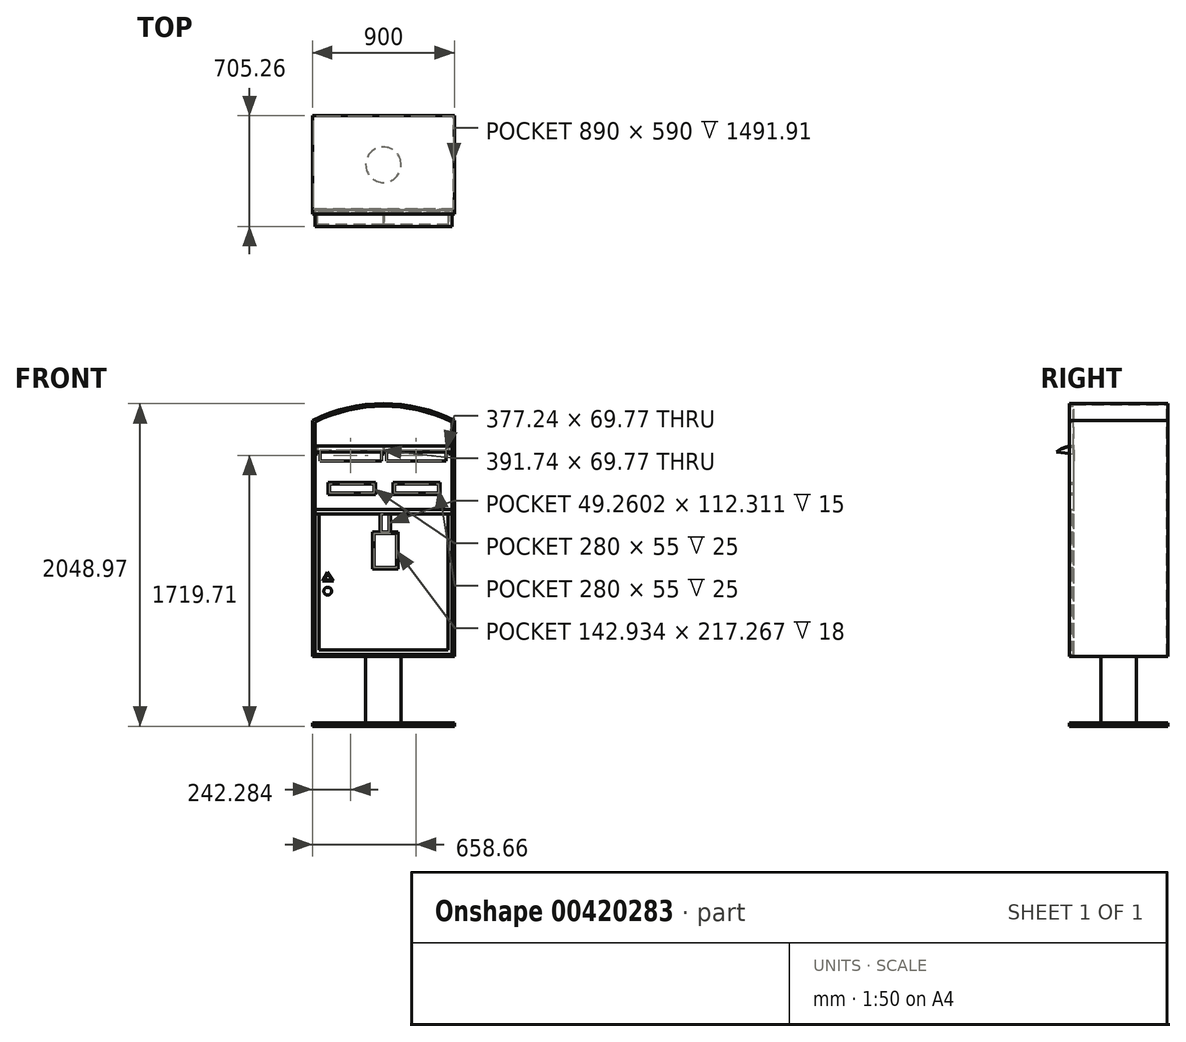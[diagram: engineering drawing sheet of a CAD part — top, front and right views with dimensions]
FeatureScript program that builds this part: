
annotation { "Feature Type Name" : "Feature", "Feature Type Description" : "" }
export const myFeature = defineFeature(function(context is Context, id is Id, definition is map)
    precondition{}
    {
        {
            var Q0;
            Q0=qCreatedBy(makeId("Front.planeOp"),FACE);
            var sketch = newSketch(context, id + "F0", { "sketchPlane" : qUnion([Q0])});
            skLineSegment(sketch, "E0.bottom", {"start": v(450, -750) * mm, "end": v(-450, -750) * mm});
            skLineSegment(sketch, "E0.left", {"start": v(450, -750) * mm, "end": v(450, 750) * mm});
            skLineSegment(sketch, "E0.right", {"start": v(-450, -750) * mm, "end": v(-450, 750) * mm});
            skPoint(sketch, "E0.middle", {"position": v(0, 0) * mm});
            skArc(sketch, "E1", {"start": v(450, 750) * mm, "mid": v(0, 856.97) * mm, "end": v(-450, 750) * mm});
            skLineSegment(sketch, "E2", {"start": v(-450, 750) * mm, "end": v(450, 750) * mm, "construction": true});
            skSolve(sketch);
        }
        {
            var Q0;
            Q0=makeQuery(id+"F0.imprint","IMPRINT",FACE,{"disambiguationData":[TD([[makeQuery(id+"F0.imprint","IMPRINT",EDGE,{"derivedFrom":sQuery(id+"F0.wireOp",EDGE,"E0.bottom")}),-1.0]])]});
            extrude(context, id + "F1", {"entities" : qUnion([Q0]), "depth" : 600 * mm});
        }
        {
            var Q0;
            Q0=makeQuery(id+"F1.opExtrude","CAP_FACE",FACE,{"disambiguationData":[OSD([sQuery(id+"F0.wireOp",EDGE,"E0.bottom"),sQuery(id+"F0.wireOp",EDGE,"E0.left"),sQuery(id+"F0.wireOp",EDGE,"E0.right"),sQuery(id+"F0.wireOp",EDGE,"E1")])],"isStart":true});
            shell(context, id + "F2", {"entities" : qUnion([Q0]), "thickness" : 5 * mm});
        }
        {
            var Q0;
            Q0=makeQuery(id+"F1.opExtrude","CAP_FACE",FACE,{"disambiguationData":[OSD([sQuery(id+"F0.wireOp",EDGE,"E0.bottom"),sQuery(id+"F0.wireOp",EDGE,"E0.left"),sQuery(id+"F0.wireOp",EDGE,"E0.right"),sQuery(id+"F0.wireOp",EDGE,"E1")])],"isStart":false});
            var sketch = newSketch(context, id + "F3", { "sketchPlane" : qUnion([Q0])});
            skLineSegment(sketch, "E3.0", {"start": v(435, -735) * mm, "end": v(435, 740.71) * mm});
            skLineSegment(sketch, "E3.1", {"start": v(-435, -735) * mm, "end": v(435, -735) * mm});
            skLineSegment(sketch, "E3.2", {"start": v(-435, 740.71) * mm, "end": v(-435, -735) * mm});
            skArc(sketch, "E3.3", {"start": v(435, 740.71) * mm, "mid": v(0, 841.97) * mm, "end": v(-435, 740.71) * mm});
            skSolve(sketch);
        }
        {
            var Q0;
            Q0=makeQuery(id+"F3.imprint","IMPRINT",FACE,{"disambiguationData":[TD([[makeQuery(id+"F3.imprint","IMPRINT",EDGE,{"derivedFrom":sQuery(id+"F3.wireOp",EDGE,"E3.0")}),-1.0]])]});
            extrude(context, id + "F4", {"entities" : qUnion([Q0]), "operationType" : NewBodyOperationType.ADD, "depth" : 25 * mm});
        }
        {
            var Q0;
            Q0=makeQuery(id+"F1.opExtrude","CAP_FACE",FACE,{"disambiguationData":[OSD([sQuery(id+"F0.wireOp",EDGE,"E0.bottom"),sQuery(id+"F0.wireOp",EDGE,"E0.left"),sQuery(id+"F0.wireOp",EDGE,"E0.right"),sQuery(id+"F0.wireOp",EDGE,"E1")])],"isStart":false});
            var sketch = newSketch(context, id + "F5", { "sketchPlane" : qUnion([Q0])});
            skLineSegment(sketch, "E4.bottom", {"start": v(-350.88, 356.23) * mm, "end": v(-50.88, 356.23) * mm});
            skLineSegment(sketch, "E4.top", {"start": v(-350.88, 281.23) * mm, "end": v(-50.88, 281.23) * mm});
            skLineSegment(sketch, "E4.left", {"start": v(-350.88, 356.23) * mm, "end": v(-350.88, 281.23) * mm});
            skLineSegment(sketch, "E4.right", {"start": v(-50.88, 356.23) * mm, "end": v(-50.88, 281.23) * mm});
            skLineSegment(sketch, "E5.bottom", {"start": v(61.2, 356.23) * mm, "end": v(361.2, 356.23) * mm});
            skLineSegment(sketch, "E5.top", {"start": v(61.2, 281.23) * mm, "end": v(361.2, 281.23) * mm});
            skLineSegment(sketch, "E5.left", {"start": v(61.2, 356.23) * mm, "end": v(61.2, 281.23) * mm});
            skLineSegment(sketch, "E5.right", {"start": v(361.2, 356.23) * mm, "end": v(361.2, 281.23) * mm});
            skLineSegment(sketch, "E6", {"start": v(-50.88, 356.23) * mm, "end": v(61.2, 356.23) * mm, "construction": true});
            skLineSegment(sketch, "E7.0", {"start": v(-340.88, 346.23) * mm, "end": v(-60.88, 346.23) * mm});
            skLineSegment(sketch, "E7.1", {"start": v(-340.88, 346.23) * mm, "end": v(-340.88, 291.23) * mm});
            skLineSegment(sketch, "E7.2", {"start": v(-340.88, 291.23) * mm, "end": v(-60.88, 291.23) * mm});
            skLineSegment(sketch, "E7.3", {"start": v(-60.88, 346.23) * mm, "end": v(-60.88, 291.23) * mm});
            skLineSegment(sketch, "E8.0", {"start": v(351.2, 346.23) * mm, "end": v(351.2, 291.23) * mm});
            skLineSegment(sketch, "E8.1", {"start": v(71.2, 346.23) * mm, "end": v(351.2, 346.23) * mm});
            skLineSegment(sketch, "E8.2", {"start": v(71.2, 346.23) * mm, "end": v(71.2, 291.23) * mm});
            skLineSegment(sketch, "E8.3", {"start": v(71.2, 291.23) * mm, "end": v(351.2, 291.23) * mm});
            skSolve(sketch);
        }
        {
            var Q0;
            Q0=makeQuery(id+"F5.imprint","IMPRINT",FACE,{"disambiguationData":[TD([[makeQuery(id+"F5.imprint","IMPRINT",EDGE,{"derivedFrom":sQuery(id+"F5.wireOp",EDGE,"E4.bottom")}),-1.0]])]});
            var Q1;
            Q1=makeQuery(id+"F5.imprint","IMPRINT",FACE,{"disambiguationData":[TD([[makeQuery(id+"F5.imprint","IMPRINT",EDGE,{"derivedFrom":sQuery(id+"F5.wireOp",EDGE,"E5.bottom")}),-1.0]])]});
            extrude(context, id + "F6", {"entities" : qUnion([Q0, Q1]), "operationType" : NewBodyOperationType.ADD, "depth" : 25 * mm});
        }
        {
            var Q0;
            Q0=makeQuery(id+"F6.boolean.opBoolean","SPLIT",FACE,{"disambiguationData":[TD([makeQuery(id+"F4.opExtrude","SWEPT_FACE",FACE,{"disambiguationData":[OSD([sQuery(id+"F3.wireOp",EDGE,"E3.0")])]})])],"derivedFrom":makeQuery(id+"F1.opExtrude","CAP_FACE",FACE,{"disambiguationData":[OSD([sQuery(id+"F0.wireOp",EDGE,"E0.bottom"),sQuery(id+"F0.wireOp",EDGE,"E0.left"),sQuery(id+"F0.wireOp",EDGE,"E0.right"),sQuery(id+"F0.wireOp",EDGE,"E1")])],"isStart":false})});
            var sketch = newSketch(context, id + "F7", { "sketchPlane" : qUnion([Q0])});
            skLineSegment(sketch, "E9.bottom", {"start": v(-435, 185.2) * mm, "end": v(435, 185.2) * mm});
            skLineSegment(sketch, "E9.top", {"start": v(-435, 155.2) * mm, "end": v(435, 155.2) * mm});
            skLineSegment(sketch, "E9.left", {"start": v(-435, 185.2) * mm, "end": v(-435, 155.2) * mm});
            skLineSegment(sketch, "E9.right", {"start": v(435, 185.2) * mm, "end": v(435, 155.2) * mm});
            skSolve(sketch);
        }
        {
            var Q0;
            Q0=makeQuery(id+"F7.imprint","IMPRINT",FACE,{"disambiguationData":[TD([[makeQuery(id+"F7.imprint","IMPRINT",EDGE,{"derivedFrom":sQuery(id+"F7.wireOp",EDGE,"E9.bottom")}),-1.0]])]});
            extrude(context, id + "F8", {"entities" : qUnion([Q0]), "operationType" : NewBodyOperationType.ADD, "depth" : 15 * mm});
        }
        {
            var Q0;
            {var subQ0=makeQuery(id+"F4.opExtrude","SWEPT_FACE",FACE,{"disambiguationData":[OSD([sQuery(id+"F3.wireOp",EDGE,"E3.0")])]});var subQ1=makeQuery(id+"F4.opExtrude","SWEPT_FACE",FACE,{"disambiguationData":[OSD([sQuery(id+"F3.wireOp",EDGE,"E3.1")])]});Q0=makeQuery(id+"F8.boolean.opBoolean","SPLIT",FACE,{"disambiguationData":[TD([subQ1])],"derivedFrom":makeQuery(id+"F6.boolean.opBoolean","SPLIT",FACE,{"disambiguationData":[TD([subQ0])],"derivedFrom":makeQuery(id+"F1.opExtrude","CAP_FACE",FACE,{"disambiguationData":[OSD([sQuery(id+"F0.wireOp",EDGE,"E0.bottom"),sQuery(id+"F0.wireOp",EDGE,"E0.left"),sQuery(id+"F0.wireOp",EDGE,"E0.right"),sQuery(id+"F0.wireOp",EDGE,"E1")])],"isStart":false})})});}
            var sketch = newSketch(context, id + "F9", { "sketchPlane" : qUnion([Q0])});
            skLineSegment(sketch, "E10.bottom", {"start": v(-22.9, 155.2) * mm, "end": v(-14.58, 155.2) * mm});
            skLineSegment(sketch, "E10.left", {"start": v(-22.9, 155.2) * mm, "end": v(-22.9, 42.9) * mm});
            skLineSegment(sketch, "E10.right", {"start": v(-14.58, 155.2) * mm, "end": v(-14.58, 42.9) * mm});
            skLineSegment(sketch, "E11.bottom", {"start": v(34.68, 155.2) * mm, "end": v(44.06, 155.2) * mm});
            skLineSegment(sketch, "E11.left", {"start": v(34.68, 155.2) * mm, "end": v(34.68, 42.9) * mm});
            skLineSegment(sketch, "E11.right", {"start": v(44.06, 155.2) * mm, "end": v(44.06, 42.9) * mm});
            skLineSegment(sketch, "E12.bottom", {"start": v(-69.05, 42.9) * mm, "end": v(-22.9, 42.9) * mm});
            skLineSegment(sketch, "E12.top", {"start": v(-69.05, -194.37) * mm, "end": v(93.89, -194.37) * mm});
            skLineSegment(sketch, "E12.left", {"start": v(-69.05, 42.9) * mm, "end": v(-69.05, -194.37) * mm});
            skLineSegment(sketch, "E12.right", {"start": v(93.89, 42.9) * mm, "end": v(93.89, -194.37) * mm});
            skLineSegment(sketch, "E13.0", {"start": v(-59.05, 32.9) * mm, "end": v(83.89, 32.9) * mm});
            skLineSegment(sketch, "E13.1", {"start": v(-59.05, 32.9) * mm, "end": v(-59.05, -184.37) * mm});
            skLineSegment(sketch, "E13.2", {"start": v(-59.05, -184.37) * mm, "end": v(83.89, -184.37) * mm});
            skLineSegment(sketch, "E13.3", {"start": v(83.89, 32.9) * mm, "end": v(83.89, -184.37) * mm});
            skLineSegment(sketch, "E14.trimOffspring", {"start": v(-14.58, 42.9) * mm, "end": v(34.68, 42.9) * mm});
            skLineSegment(sketch, "E15.trimOffspring", {"start": v(44.06, 42.9) * mm, "end": v(93.89, 42.9) * mm});
            skSolve(sketch);
        }
        {
            var Q0;
            Q0=makeQuery(id+"F9.imprint","IMPRINT",FACE,{"disambiguationData":[TD([[makeQuery(id+"F9.imprint","IMPRINT",EDGE,{"derivedFrom":sQuery(id+"F9.wireOp",EDGE,"E10.bottom")}),-1.0]])]});
            extrude(context, id + "F10", {"entities" : qUnion([Q0]), "operationType" : NewBodyOperationType.ADD, "depth" : 18 * mm});
        }
        {
            var Q0;
            {var subQ0=makeQuery(id+"F4.opExtrude","SWEPT_FACE",FACE,{"disambiguationData":[OSD([sQuery(id+"F3.wireOp",EDGE,"E3.0")])]});var subQ1=makeQuery(id+"F4.opExtrude","SWEPT_FACE",FACE,{"disambiguationData":[OSD([sQuery(id+"F3.wireOp",EDGE,"E3.1")])]});Q0=makeQuery(id+"F10.boolean.opBoolean","SPLIT",FACE,{"disambiguationData":[TD([subQ0])],"derivedFrom":makeQuery(id+"F8.boolean.opBoolean","SPLIT",FACE,{"disambiguationData":[TD([subQ1])],"derivedFrom":makeQuery(id+"F6.boolean.opBoolean","SPLIT",FACE,{"disambiguationData":[TD([subQ0])],"derivedFrom":makeQuery(id+"F1.opExtrude","CAP_FACE",FACE,{"disambiguationData":[OSD([sQuery(id+"F0.wireOp",EDGE,"E0.bottom"),sQuery(id+"F0.wireOp",EDGE,"E0.left"),sQuery(id+"F0.wireOp",EDGE,"E0.right"),sQuery(id+"F0.wireOp",EDGE,"E1")])],"isStart":false})})})});}
            var sketch = newSketch(context, id + "F11", { "sketchPlane" : qUnion([Q0])});
            skLineSegment(sketch, "E16.bottom", {"start": v(-408.64, 155.2) * mm, "end": v(408.76, 155.2) * mm});
            skLineSegment(sketch, "E16.top", {"start": v(-408.64, -707.83) * mm, "end": v(408.76, -707.83) * mm});
            skLineSegment(sketch, "E16.left", {"start": v(-408.64, 155.2) * mm, "end": v(-408.64, -707.83) * mm});
            skLineSegment(sketch, "E16.right", {"start": v(408.76, 155.2) * mm, "end": v(408.76, -707.83) * mm});
            skSolve(sketch);
        }
        {
            var Q0;
            Q0=makeQuery(id+"F11.imprint","IMPRINT",FACE,{"disambiguationData":[TD([[makeQuery(id+"F11.imprint","IMPRINT",EDGE,{"derivedFrom":sQuery(id+"F11.wireOp",EDGE,"E16.top")}),1.0]])]});
            extrude(context, id + "F12", {"entities" : qUnion([Q0]), "operationType" : NewBodyOperationType.ADD, "depth" : 12 * mm});
        }
        {
            var Q0;
            Q0=makeQuery(id+"F12.opExtrude","CAP_FACE",FACE,{"disambiguationData":[OSD([sQuery(id+"F9.wireOp",EDGE,"E10.left"),sQuery(id+"F9.wireOp",EDGE,"E11.right"),sQuery(id+"F9.wireOp",EDGE,"E12.bottom"),sQuery(id+"F9.wireOp",EDGE,"E12.top"),sQuery(id+"F9.wireOp",EDGE,"E12.left"),sQuery(id+"F9.wireOp",EDGE,"E12.right"),sQuery(id+"F9.wireOp",EDGE,"E15.trimOffspring"),sQuery(id+"F11.wireOp",EDGE,"E16.bottom"),sQuery(id+"F11.wireOp",EDGE,"E16.top"),sQuery(id+"F11.wireOp",EDGE,"E16.left"),sQuery(id+"F11.wireOp",EDGE,"E16.right")])],"isStart":false});
            var sketch = newSketch(context, id + "F13", { "sketchPlane" : qUnion([Q0])});
            skCircle(sketch, "E17", {"center": v(-354.07, -333.63) * mm, "radius": 24.86 * mm});
            skSolve(sketch);
        }
        {
            var Q0;
            Q0 = qSketchRegion(id + "F13", true);
            extrude(context, id + "F14", {"entities" : qUnion([Q0]), "operationType" : NewBodyOperationType.ADD, "depth" : 5 * mm});
        }
        {
            var Q0;
            Q0=makeQuery(id+"F12.opExtrude","CAP_FACE",FACE,{"disambiguationData":[OSD([sQuery(id+"F9.wireOp",EDGE,"E10.left"),sQuery(id+"F9.wireOp",EDGE,"E11.right"),sQuery(id+"F9.wireOp",EDGE,"E12.bottom"),sQuery(id+"F9.wireOp",EDGE,"E12.top"),sQuery(id+"F9.wireOp",EDGE,"E12.left"),sQuery(id+"F9.wireOp",EDGE,"E12.right"),sQuery(id+"F9.wireOp",EDGE,"E15.trimOffspring"),sQuery(id+"F11.wireOp",EDGE,"E16.bottom"),sQuery(id+"F11.wireOp",EDGE,"E16.top"),sQuery(id+"F11.wireOp",EDGE,"E16.left"),sQuery(id+"F11.wireOp",EDGE,"E16.right")])],"isStart":false});
            var sketch = newSketch(context, id + "F15", { "sketchPlane" : qUnion([Q0])});
            skLineSegment(sketch, "E18", {"start": v(-353.42, -222.08) * mm, "end": v(-378.96, -263.68) * mm});
            skLineSegment(sketch, "E19", {"start": v(-378.96, -263.68) * mm, "end": v(-325.69, -263.68) * mm});
            skLineSegment(sketch, "E20", {"start": v(-325.69, -263.68) * mm, "end": v(-353.42, -222.08) * mm});
            skLineSegment(sketch, "E21.0", {"start": v(-316.35, -268.68) * mm, "end": v(-353.6, -212.8) * mm});
            skLineSegment(sketch, "E21.1", {"start": v(-387.9, -268.68) * mm, "end": v(-316.35, -268.68) * mm});
            skLineSegment(sketch, "E21.2", {"start": v(-353.6, -212.8) * mm, "end": v(-387.9, -268.68) * mm});
            skSolve(sketch);
        }
        {
            var Q0;
            Q0=makeQuery(id+"F15.imprint","IMPRINT",FACE,{"disambiguationData":[TD([[makeQuery(id+"F15.imprint","IMPRINT",EDGE,{"derivedFrom":sQuery(id+"F15.wireOp",EDGE,"E18")}),-1.0]])]});
            extrude(context, id + "F16", {"entities" : qUnion([Q0]), "operationType" : NewBodyOperationType.ADD, "depth" : 10 * mm});
        }
        {
            var Q0;
            Q0=makeQuery(id+"F4.opExtrude","SWEPT_FACE",FACE,{"disambiguationData":[OSD([sQuery(id+"F3.wireOp",EDGE,"E3.2")])]});
            var sketch = newSketch(context, id + "F17", { "sketchPlane" : qUnion([Q0])});
            skArc(sketch, "E22", {"start": v(-600, 589.22) * mm, "mid": v(-655.37, 577.85) * mm, "end": v(-705.26, 551.27) * mm});
            skLineSegment(sketch, "E23", {"start": v(-705.26, 551.27) * mm, "end": v(-693.41, 549.79) * mm});
            skLineSegment(sketch, "E24", {"start": v(-600, 581.2) * mm, "end": v(-600, 589.22) * mm});
            skArc(sketch, "E25.0", {"start": v(-599.53, 581.23) * mm, "mid": v(-648.56, 571.75) * mm, "end": v(-693.41, 549.79) * mm});
            skSolve(sketch);
        }
        {
            var Q0;
            {var subQ0=sQuery(id+"F17.wireOp",EDGE,"E23");Q0=makeQuery(id+"F17.imprint","IMPRINT",FACE,{"disambiguationData":[TD([[makeQuery(id+"F17.imprint","IMPRINT",EDGE,{"derivedFrom":subQ0}),1.0]])]});}
            var Q1;
            {var subQ0=sQuery(id+"F17.wireOp",EDGE,"E24");Q1=makeQuery(id+"F17.imprint","IMPRINT",FACE,{"disambiguationData":[TD([[makeQuery(id+"F17.imprint","IMPRINT",EDGE,{"derivedFrom":subQ0}),-1.0]])]});}
            var Q2;
            Q2=makeQuery(id+"F4.opExtrude","SWEPT_FACE",FACE,{"disambiguationData":[OSD([sQuery(id+"F3.wireOp",EDGE,"E3.0")])]});
            extrude(context, id + "F18", {"entities" : qUnion([Q0, Q1]), "operationType" : NewBodyOperationType.ADD, "endBound" : BoundingType.UP_TO_SURFACE, "endBoundEntityFace" : qUnion([Q2]), "depth" : 25 * mm});
        }
        {
            var Q0;
            Q0=makeQuery(id+"F18.opExtrude","CAP_FACE",FACE,{"disambiguationData":[OSD([sQuery(id+"F17.wireOp",EDGE,"E22"),sQuery(id+"F17.wireOp",EDGE,"E23"),sQuery(id+"F17.wireOp",EDGE,"E24"),sQuery(id+"F17.wireOp",EDGE,"E25.0")])],"isStart":false});
            var sketch = newSketch(context, id + "F19", { "sketchPlane" : qUnion([Q0])});
            skLineSegment(sketch, "E26", {"start": v(-705.26, 551.27) * mm, "end": v(-600, 538.13) * mm});
            skLineSegment(sketch, "E27", {"start": v(-600, 538.13) * mm, "end": v(-600, 589.22) * mm});
            skArc(sketch, "E28.0", {"start": v(-705.26, 551.27) * mm, "mid": v(-667.08, 573.2) * mm, "end": v(-625, 586.13) * mm});
            skArc(sketch, "E29.0", {"start": v(-625, 586.13) * mm, "mid": v(-612.55, 588.07) * mm, "end": v(-600, 589.22) * mm});
            skSolve(sketch);
        }
        {
            var Q0;
            {var subQ0=sQuery(id+"F19.wireOp",EDGE,"E27");Q0=makeQuery(id+"F19.imprint","IMPRINT",FACE,{"disambiguationData":[TD([[makeQuery(id+"F19.imprint","IMPRINT",EDGE,{"derivedFrom":subQ0}),1.0]])]});}
            var Q1;
            {var subQ0=sQuery(id+"F19.wireOp",EDGE,"E28.0");Q1=makeQuery(id+"F19.imprint","IMPRINT",FACE,{"disambiguationData":[TD([[makeQuery(id+"F19.imprint","IMPRINT",EDGE,{"derivedFrom":subQ0}),-1.0]])]});}
            extrude(context, id + "F20", {"entities" : qUnion([Q0, Q1]), "operationType" : NewBodyOperationType.ADD, "oppositeDirection" : true, "depth" : 20 * mm});
        }
        {
            var Q0;
            Q0=makeQuery(id+"F18.opExtrude","CAP_FACE",FACE,{"disambiguationData":[OSD([sQuery(id+"F17.wireOp",EDGE,"E22"),sQuery(id+"F17.wireOp",EDGE,"E23"),sQuery(id+"F17.wireOp",EDGE,"E24"),sQuery(id+"F17.wireOp",EDGE,"E25.0")])],"isStart":true});
            var sketch = newSketch(context, id + "F21", { "sketchPlane" : qUnion([Q0])});
            skLineSegment(sketch, "E30.0.1", {"start": v(600, 581.2) * mm, "end": v(600, 538.13) * mm});
            skLineSegment(sketch, "E30.0.2", {"start": v(600, 538.13) * mm, "end": v(693.41, 549.79) * mm});
            skArc(sketch, "E31.0", {"start": v(625, 586.13) * mm, "mid": v(667.08, 573.2) * mm, "end": v(705.26, 551.27) * mm});
            skArc(sketch, "E32.0", {"start": v(600, 589.22) * mm, "mid": v(612.55, 588.07) * mm, "end": v(625, 586.13) * mm});
            skLineSegment(sketch, "E33", {"start": v(693.41, 549.79) * mm, "end": v(705.26, 551.27) * mm});
            skLineSegment(sketch, "E34", {"start": v(600, 589.22) * mm, "end": v(600, 581.2) * mm});
            skSolve(sketch);
        }
        {
            var Q0;
            Q0=makeQuery(id+"F21.imprint","IMPRINT",FACE,{"disambiguationData":[TD([[makeQuery(id+"F21.imprint","IMPRINT",EDGE,{"derivedFrom":sQuery(id+"F21.wireOp",EDGE,"E31.0")}),-1.0]])]});
            var Q1;
            Q1=makeQuery(id+"F21.imprint","IMPRINT",FACE,{"disambiguationData":[TD([[makeQuery(id+"F21.imprint","IMPRINT",EDGE,{"derivedFrom":sQuery(id+"F21.wireOp",EDGE,"E30.0.1")}),1.0]])]});
            extrude(context, id + "F22", {"entities" : qUnion([Q0, Q1]), "operationType" : NewBodyOperationType.ADD, "oppositeDirection" : true, "depth" : 18 * mm});
        }
        {
            var Q0;
            {var subQ0=sQuery(id+"F0.wireOp",EDGE,"E0.left");Q0=makeQuery(id+"F4.boolean.opBoolean","MERGE",FACE,{"derivedFrom":[makeQuery(id+"F1.opExtrude","SWEPT_FACE",FACE,{"disambiguationData":[OSD([subQ0])]}),makeQuery(id+"F4.opExtrude","SWEPT_FACE",FACE,{"disambiguationData":[OSD([subQ0])]})]});}
            cPlane(context, id + "F23", {"entities" : qUnion([Q0]), "cplaneType" : CPlaneType.OFFSET, "offset" : 450 * mm, "oppositeDirection" : true, "width" : 150 * mm, "height" : 150 * mm});
        }
        {
            var Q0;
            Q0=qCreatedBy(id+"F23.planeOp",FACE);
            var sketch = newSketch(context, id + "F24", { "sketchPlane" : qUnion([Q0])});
            skArc(sketch, "E35.0.0", {"start": v(-600, 581.2) * mm, "mid": v(-648.78, 571.67) * mm, "end": v(-693.41, 549.79) * mm});
            skLineSegment(sketch, "E35.0.1", {"start": v(-693.41, 549.79) * mm, "end": v(-600, 538.13) * mm});
            skLineSegment(sketch, "E35.0.2", {"start": v(-600, 538.13) * mm, "end": v(-600, 581.2) * mm});
            skSolve(sketch);
        }
        {
            var Q0;
            Q0=makeQuery(id+"F24.imprint","IMPRINT",FACE,{"disambiguationData":[TD([[makeQuery(id+"F24.imprint","IMPRINT",EDGE,{"derivedFrom":sQuery(id+"F24.wireOp",EDGE,"E35.0.0")}),1.0]])]});
            extrude(context, id + "F25", {"entities" : qUnion([Q0]), "operationType" : NewBodyOperationType.ADD, "depth" : 5 * mm});
        }
        {
            var Q0;
            Q0=makeQuery(id+"F1.opExtrude","CAP_FACE",FACE,{"disambiguationData":[OSD([sQuery(id+"F0.wireOp",EDGE,"E0.bottom"),sQuery(id+"F0.wireOp",EDGE,"E0.left"),sQuery(id+"F0.wireOp",EDGE,"E0.right"),sQuery(id+"F0.wireOp",EDGE,"E1")])],"isStart":true});
            var sketch = newSketch(context, id + "F26", { "sketchPlane" : qUnion([Q0])});
            skArc(sketch, "E36.0", {"start": v(-450, 750) * mm, "mid": v(0, 856.97) * mm, "end": v(450, 750) * mm});
            skLineSegment(sketch, "E37.0", {"start": v(-450, -750) * mm, "end": v(-450, 750) * mm});
            skLineSegment(sketch, "E38.0", {"start": v(450, -750) * mm, "end": v(450, 750) * mm});
            skLineSegment(sketch, "E39.0", {"start": v(-450, -750) * mm, "end": v(450, -750) * mm});
            skSolve(sketch);
        }
        {
            var Q0;
            {var subQ0=sQuery(id+"F0.wireOp",EDGE,"E0.bottom");Q0=makeQuery(id+"F26.imprint","IMPRINT",FACE,{"disambiguationData":[TD([[makeQuery(id+"F26.imprint","IMPRINT",EDGE,{"derivedFrom":makeQuery(id+"F2.opShell","OFFSET_EDGE",EDGE,{"disambiguationData":[OSD([subQ0]),TDD([makeQuery(id+"F1.opExtrude","CAP_EDGE",EDGE,{"disambiguationData":[OSD([subQ0])],"isStart":true})])]})}),1.0]])]});}
            extrude(context, id + "F27", {"entities" : qUnion([Q0]), "operationType" : NewBodyOperationType.ADD, "oppositeDirection" : true, "depth" : 5 * mm});
        }
        {
            var Q0;
            {var subQ4=makeQuery(id+"F4.opExtrude","SWEPT_FACE",FACE,{"disambiguationData":[OSD([sQuery(id+"F3.wireOp",EDGE,"E3.0")])]});var subQ8=makeQuery(id+"F6.opExtrude","SWEPT_FACE",FACE,{"disambiguationData":[OSD([sQuery(id+"F5.wireOp",EDGE,"E4.bottom")])]});var subQ11=makeQuery(id+"F4.opExtrude","SWEPT_FACE",FACE,{"disambiguationData":[OSD([sQuery(id+"F3.wireOp",EDGE,"E3.3")])]});Q0=makeQuery(id+"F18.boolean.opBoolean","SPLIT",FACE,{"disambiguationData":[TD([subQ8])],"derivedFrom":makeQuery(id+"F8.boolean.opBoolean","SPLIT",FACE,{"disambiguationData":[TD([subQ11])],"derivedFrom":makeQuery(id+"F6.boolean.opBoolean","SPLIT",FACE,{"disambiguationData":[TD([subQ4])],"derivedFrom":makeQuery(id+"F1.opExtrude","CAP_FACE",FACE,{"disambiguationData":[OSD([sQuery(id+"F0.wireOp",EDGE,"E0.bottom"),sQuery(id+"F0.wireOp",EDGE,"E0.left"),sQuery(id+"F0.wireOp",EDGE,"E0.right"),sQuery(id+"F0.wireOp",EDGE,"E1")])],"isStart":false})})})});}
            var sketch = newSketch(context, id + "F28", { "sketchPlane" : qUnion([Q0])});
            skLineSegment(sketch, "E40.bottom", {"start": v(-403.59, 562.6) * mm, "end": v(-11.85, 562.6) * mm});
            skLineSegment(sketch, "E40.top", {"start": v(-403.59, 492.83) * mm, "end": v(-11.85, 492.83) * mm});
            skLineSegment(sketch, "E40.left", {"start": v(-403.59, 562.6) * mm, "end": v(-403.59, 492.83) * mm});
            skLineSegment(sketch, "E40.right", {"start": v(-11.85, 562.6) * mm, "end": v(-11.85, 492.83) * mm});
            skLineSegment(sketch, "E41.bottom", {"start": v(20.04, 562.6) * mm, "end": v(397.28, 562.6) * mm});
            skLineSegment(sketch, "E41.top", {"start": v(20.04, 492.83) * mm, "end": v(397.28, 492.83) * mm});
            skLineSegment(sketch, "E41.left", {"start": v(20.04, 562.6) * mm, "end": v(20.04, 492.83) * mm});
            skLineSegment(sketch, "E41.right", {"start": v(397.28, 562.6) * mm, "end": v(397.28, 492.83) * mm});
            skLineSegment(sketch, "E42", {"start": v(-11.85, 562.6) * mm, "end": v(20.04, 562.6) * mm, "construction": true});
            skLineSegment(sketch, "E43", {"start": v(-11.85, 492.83) * mm, "end": v(20.04, 492.83) * mm, "construction": true});
            skSolve(sketch);
        }
        {
            var Q0;
            Q0=makeQuery(id+"F28.imprint","IMPRINT",FACE,{"disambiguationData":[TD([[makeQuery(id+"F28.imprint","IMPRINT",EDGE,{"derivedFrom":sQuery(id+"F28.wireOp",EDGE,"E40.bottom")}),-1.0]])]});
            var Q1;
            Q1=makeQuery(id+"F28.imprint","IMPRINT",FACE,{"disambiguationData":[TD([[makeQuery(id+"F28.imprint","IMPRINT",EDGE,{"derivedFrom":sQuery(id+"F28.wireOp",EDGE,"E41.bottom")}),-1.0]])]});
            extrude(context, id + "F29", {"entities" : qUnion([Q0, Q1]), "operationType" : NewBodyOperationType.REMOVE, "oppositeDirection" : true, "depth" : 25 * mm});
        }
        {
            var Q0;
            {var subQ0=sQuery(id+"F0.wireOp",EDGE,"E0.bottom");Q0=makeQuery(id+"F4.boolean.opBoolean","MERGE",FACE,{"derivedFrom":[makeQuery(id+"F1.opExtrude","SWEPT_FACE",FACE,{"disambiguationData":[OSD([subQ0])]}),makeQuery(id+"F4.opExtrude","SWEPT_FACE",FACE,{"disambiguationData":[OSD([subQ0])]})]});}
            var sketch = newSketch(context, id + "F30", { "sketchPlane" : qUnion([Q0])});
            skCircle(sketch, "E44", {"center": v(0, 312.5) * mm, "radius": 112.5 * mm});
            skPoint(sketch, "E44.centerSnap0", {"position": v(-450, 312.5) * mm});
            skPoint(sketch, "E44.centerSnap1", {"position": v(0, 625) * mm});
            skSolve(sketch);
        }
        {
            var Q0;
            Q0 = qSketchRegion(id + "F30", true);
            extrude(context, id + "F31", {"entities" : qUnion([Q0]), "operationType" : NewBodyOperationType.ADD, "depth" : 422 * mm});
        }
        {
            var Q0;
            Q0=makeQuery(id+"F31.opExtrude","CAP_FACE",FACE,{"disambiguationData":[OSD([sQuery(id+"F30.wireOp",EDGE,"E44")])],"isStart":false});
            var sketch = newSketch(context, id + "F32", { "sketchPlane" : qUnion([Q0])});
            skLineSegment(sketch, "E45.0.0", {"start": v(-450, 0) * mm, "end": v(450, 0) * mm});
            skLineSegment(sketch, "E45.0.1", {"start": v(450, 0) * mm, "end": v(450, 625) * mm});
            skLineSegment(sketch, "E45.0.2", {"start": v(450, 625) * mm, "end": v(-450, 625) * mm});
            skLineSegment(sketch, "E45.0.3", {"start": v(-450, 625) * mm, "end": v(-450, 0) * mm});
            skSolve(sketch);
        }
        {
            var Q0;
            Q0=makeQuery(id+"F32.imprint","IMPRINT",FACE,{"disambiguationData":[TD([[makeQuery(id+"F32.imprint","IMPRINT",EDGE,{"derivedFrom":sQuery(id+"F32.wireOp",EDGE,"E45.0.0")}),1.0]])]});
            var Q1;
            Q1=makeQuery(id+"F32.imprint","IMPRINT",FACE,{"disambiguationData":[TD([[makeQuery(id+"F32.imprint","IMPRINT",EDGE,{"derivedFrom":makeQuery(id+"F31.opExtrude","CAP_EDGE",EDGE,{"disambiguationData":[OSD([sQuery(id+"F30.wireOp",EDGE,"E44")])],"isStart":false})}),1.0]])]});
            extrude(context, id + "F33", {"entities" : qUnion([Q0, Q1]), "operationType" : NewBodyOperationType.ADD, "depth" : 20 * mm});
        }
    });
